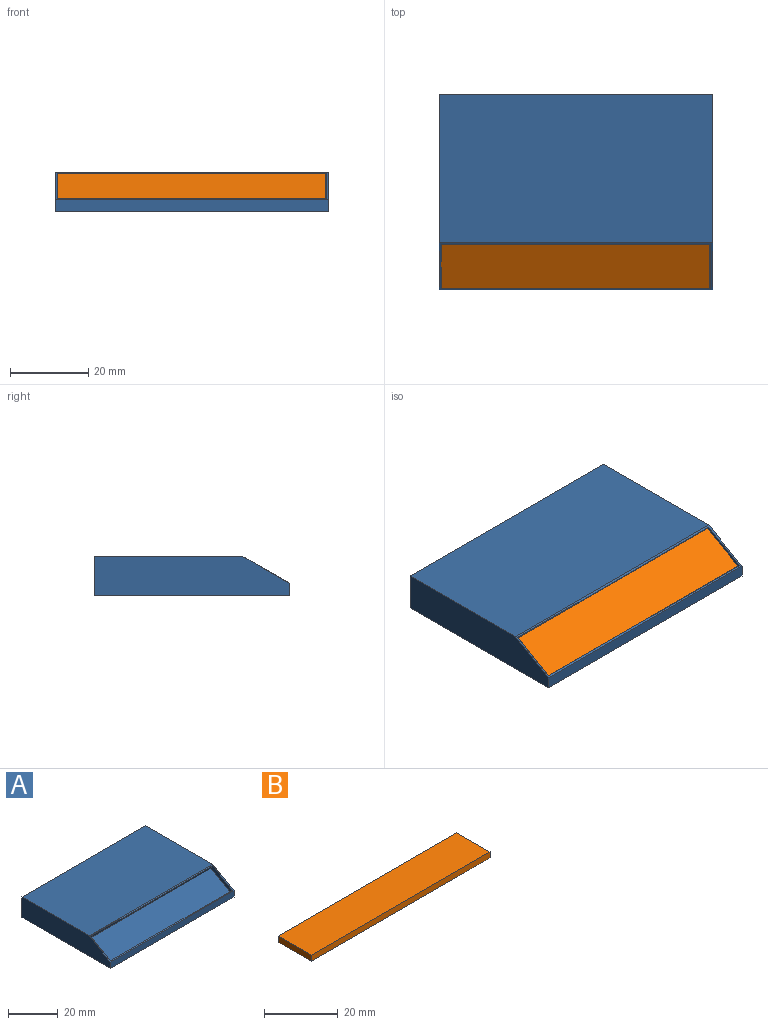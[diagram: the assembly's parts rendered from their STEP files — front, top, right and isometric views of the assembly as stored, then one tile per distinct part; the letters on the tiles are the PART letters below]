
ASSEMBLY  parts=2 mates=1
PART A: 12 faces, bbox 70x50x10 mm
  f0: plane 70x10mm, normal (0,1,0), area 700mm2, adj f1,f3,f4,f5
  f1: plane 50x10mm, normal (-1,0,0), area 458.4mm2, adj f0,f2,f4,f5,f6
  f2: plane 70x3.07mm, normal (0,-1,0), area 215mm2, adj f1,f3,f5,f6
  f3: plane 50x10mm, normal (1,0,0), area 458.4mm2, adj f0,f2,f4,f5,f6
  f4: plane 70x38mm, normal (0,0,1), area 2660mm2, adj f0,f1,f3,f6
  f5: plane 70x50mm, normal (0,0,-1), area 3500mm2, adj f0,f1,f2,f3
  f6: plane 70x12mm, normal (0,-0.5,0.87), area 82.9mm2, adj f1,f2,f3,f4,f7,f8,f9,f10
  f7: plane 12.13x8.16mm, normal (1,0,0), area 25.7mm2, adj f6,f8,f10,f11
  f8: plane 69x1.73mm, normal (0,0.87,0.5), area 138mm2, adj f6,f7,f9,f11
  f9: plane 12.13x8.16mm, normal (-1,0,0), area 25.7mm2, adj f6,f8,f10,f11
  f10: plane 69x1.73mm, normal (0,-0.87,-0.5), area 138mm2, adj f6,f7,f9,f11
  f11: plane 69x11.13mm, normal (0,-0.5,0.87), area 887.1mm2, adj f7,f8,f9,f10
PART B: 6 faces, bbox 68.5x12.7x2 mm
  f0: plane 68.5x2mm, normal (0,1,0), area 137mm2, adj f1,f3,f4,f5
  f1: plane 12.7x2mm, normal (-1,0,0), area 25.4mm2, adj f0,f2,f4,f5
  f2: plane 68.5x2mm, normal (0,-1,0), area 137mm2, adj f1,f3,f4,f5
  f3: plane 12.7x2mm, normal (1,0,0), area 25.4mm2, adj f0,f2,f4,f5
  f4: plane 68.5x12.7mm, normal (0,0,1), area 870mm2, adj f0,f1,f2,f3
  f5: plane 68.5x12.7mm, normal (0,0,-1), area 870mm2, adj f0,f1,f2,f3
PLACE A at identity
PLACE B rot(axis=(1,0,0),30deg) t=(2.82,-12.06,5.19)mm
MATE planar B.f5 <-> A.f11  axis (0,0.5,-0.87) through (4.89,-12.78,4.78)mm
